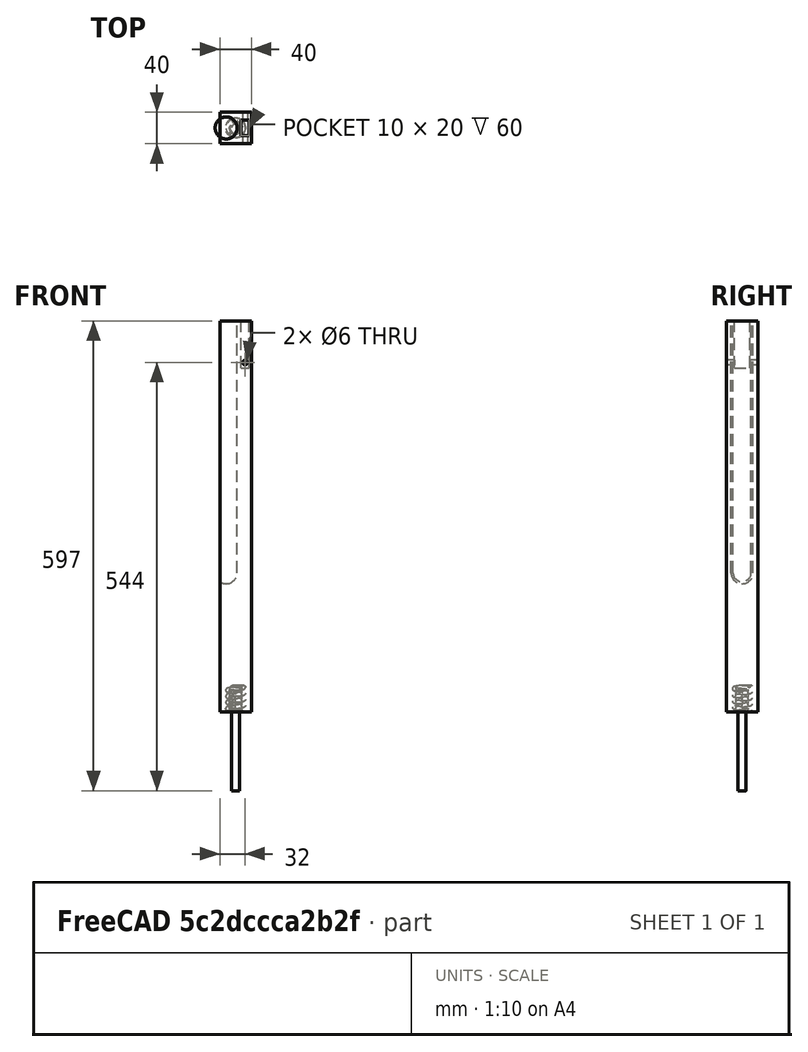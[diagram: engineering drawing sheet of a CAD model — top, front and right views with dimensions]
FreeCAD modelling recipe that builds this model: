
FCSTD DOCUMENT  (FreeCAD 0.16R6704 (Git))
Label: Pieza grande del medio2
License: All rights reserved
LicenseURL: http://en.wikipedia.org/wiki/All_rights_reserved
objects: Part::Cut×7, Part::Box×4, Part::Cylinder×3, Part::Sweep×1, Part::Sphere×1, Part::MultiFuse×1
note: 17 computed .brp shape members not serialized (recipe doc carries the construction recipe); baked Part::Feature solids carry a one-line shape summary decoded from their .brp

FEATURE [Part::Box] Box111  label="Cub principal002"
  Height = 497
  Length = 40
  Placement = pos=(0,-20,88) rot=(0,0,1;0rad)
  Width = 40
FEATURE [Part::Cylinder] Cylinder181  label="cilindro de seguridad002"
  Angle = 360
  Height = 320
  Placement = pos=(8,0,265) rot=(0,0,1;0rad)
  Radius = 14
FEATURE [Part::Box] Box112  label="Agujero del saliente002"
  Height = 60
  Length = 10
  Placement = pos=(27,-10,525) rot=(0,0,1;0rad)
  Width = 20
FEATURE [Part::Cylinder] Cylinder182  label="Pasador002"
  Angle = 360
  Height = 60
  Placement = pos=(32,30,532) rot=(1,0,0;1.5708rad)
  Radius = 3
FEATURE [Part::Cut] Cut223
  Base = -> Box111
  Tool = -> Cylinder181
FEATURE [Part::Cut] Cut224
  Base = -> Cut223
  Tool = -> Box112
FEATURE [Part::Cut] Cut225
  Base = -> Cut224
  Tool = -> Cylinder182
FEATURE [Part::Cylinder] Cylinder183  label="saliente del amortiguador001"
  Angle = 360
  Height = 120
  Placement = pos=(20,0,-12) rot=(0,0,1;0rad)
  Radius = 5
FEATURE [Part::Sweep] Sweep009
  Frenet = true
  Placement = pos=(4,-76,0) rot=(0,0,-1;1.5708rad)
  Solid = true
  Transition = 1
FEATURE [Part::Box] Box113  label="Cubo077"
  Height = 6
  Length = 27
  Placement = pos=(0,-89,-6) rot=(0,0,1;0rad)
  Width = 25
FEATURE [Part::Cut] Cut226
  Base = -> Sweep009
  Tool = -> Box113
FEATURE [Part::Box] Box114  label="Cubo078"
  Height = 29
  Length = 32
  Placement = pos=(-9,-89,105) rot=(0,0,1;0rad)
  Width = 27
FEATURE [Part::Cut] Cut227  label="EL AMORTIGUADOR008"
  Base = -> Cut226
  Placement = pos=(16,76,17) rot=(0,0,1;0rad)
  Tool = -> Box114
FEATURE [Part::Sphere] Sphere016  label="esfera de seguridad013"
  Angle1 = -90
  Angle2 = 90
  Angle3 = 360
  Placement = pos=(8,0,265) rot=(0,0,1;0rad)
  Radius = 14
FEATURE [Part::Cut] Cut228
  Base = -> Cut225
  Tool = -> Sphere016
FEATURE [Part::MultiFuse] Fusion056
  Shapes = -> [Cylinder183,Cut228]
FEATURE [Part::Cut] Cut229  label="Pieza grande del medio001"
  Base = -> Fusion056
  Placement = pos=(-50,460,0) rot=(0,0,1;0rad)
  Tool = -> Cut227
